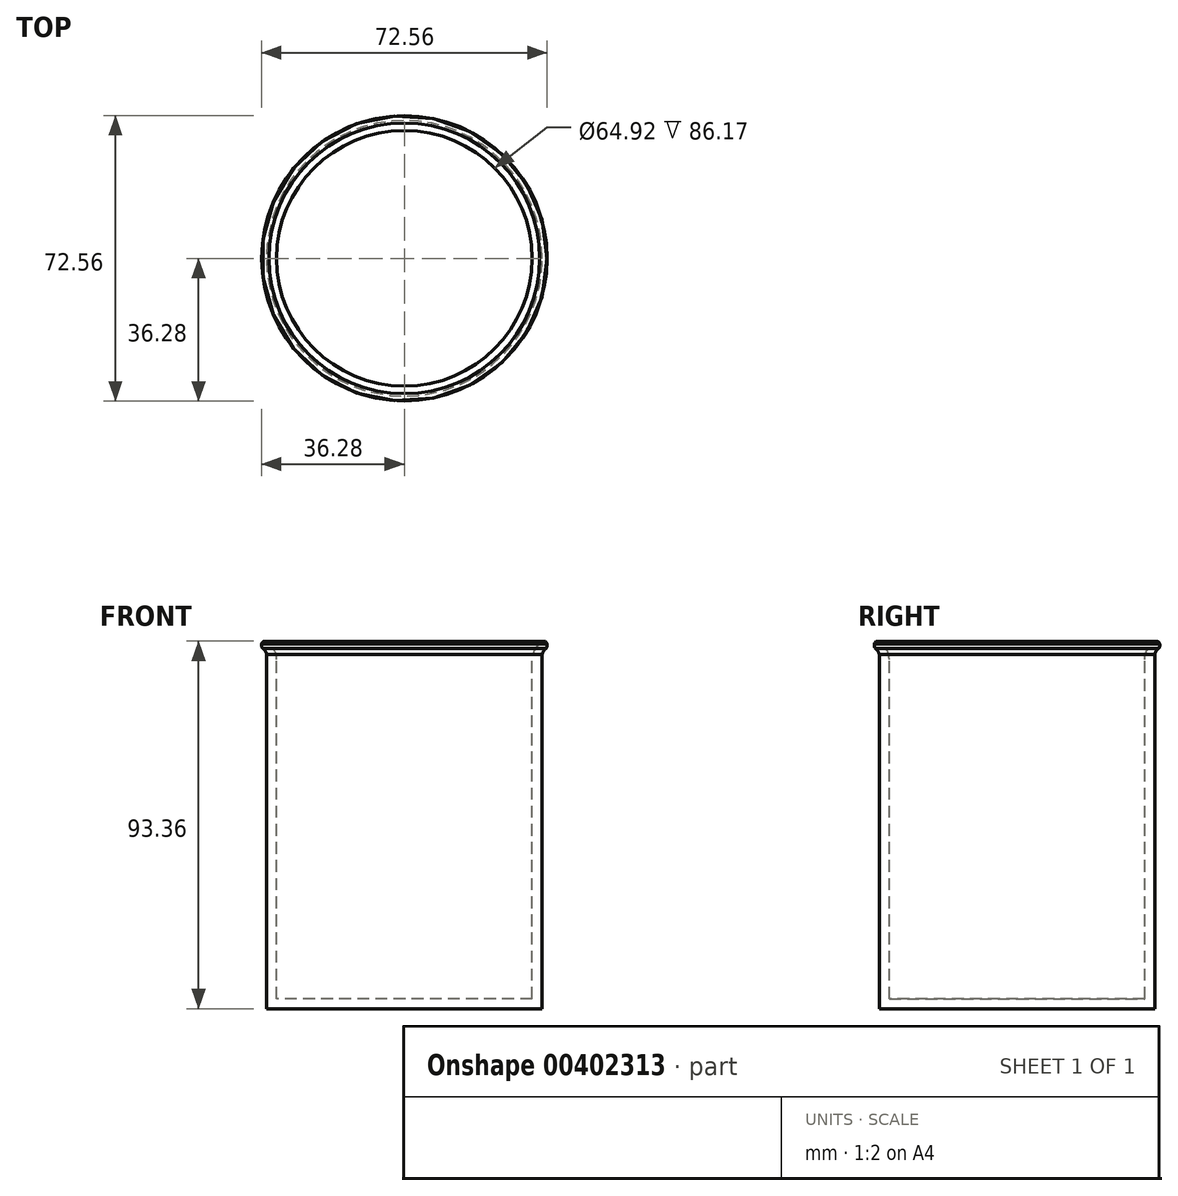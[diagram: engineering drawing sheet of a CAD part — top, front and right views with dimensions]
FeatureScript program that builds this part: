
annotation { "Feature Type Name" : "Feature", "Feature Type Description" : "" }
export const myFeature = defineFeature(function(context is Context, id is Id, definition is map)
    precondition{}
    {
        {
            var Q0;
            Q0=qCreatedBy(makeId("Front.planeOp"),FACE);
            var sketch = newSketch(context, id + "F0", { "sketchPlane" : qUnion([Q0])});
            skLineSegment(sketch, "E0.0", {"start": v(0, 45) * mm, "end": v(35, 45) * mm});
            skPoint(sketch, "E1", {"position": v(0, 45) * mm});
            skFitSpline(sketch, "E2", {"points": [v(35, 45) * mm, v(35.3, 45.79) * mm, v(35.98, 46.5) * mm], "startDerivative": vector(0.03, 0.4) * mm, "endDerivative": vector(0.23, 0.06) * mm});
            skLineSegment(sketch, "E3", {"start": v(35.98, 46.5) * mm, "end": v(0, 46.5) * mm});
            skLineSegment(sketch, "E4", {"start": v(0, 46.5) * mm, "end": v(0, 45) * mm});
            skFitSpline(sketch, "E5", {"points": [v(35.98, 46.5) * mm, v(36.23, 46.97) * mm, v(36.25, 47.7) * mm], "startDerivative": vector(0.12, 0.14) * mm, "endDerivative": vector(-0.1, 0.12) * mm});
            skPoint(sketch, "E6.endSnap0", {"position": v(18, 46.5) * mm});
            skLineSegment(sketch, "E7", {"start": v(34.4, 47.7) * mm, "end": v(0, 47.7) * mm});
            skLineSegment(sketch, "E8", {"start": v(0, 47.7) * mm, "end": v(0, 46.5) * mm});
            skFitSpline(sketch, "E9", {"points": [v(34.4, 47.7) * mm, v(34.6, 48.2) * mm, v(35.86, 48.26) * mm, v(36.25, 47.7) * mm], "startDerivative": vector(0.9, 3.73) * mm, "endDerivative": vector(0.6, -1) * mm});
            skLineSegment(sketch, "E10.0", {"start": v(0, -45) * mm, "end": v(35, -45) * mm});
            skLineSegment(sketch, "E11", {"start": v(35, -45) * mm, "end": v(0, -45) * mm});
            skLineSegment(sketch, "E12", {"start": v(0, -45) * mm, "end": v(0, 45) * mm});
            skLineSegment(sketch, "E13", {"start": v(35, 45) * mm, "end": v(35, -45) * mm});
            skSolve(sketch);
        }
        {
            var Q0;
            Q0 = qSketchRegion(id + "F0", true);
            var Q1;
            Q1=sQuery(id+"F0.wireOp",EDGE,"E4");
            revolve(context, id + "F1", {"entities" : qUnion([Q0]), "axis" : qUnion([Q1]), "revolveType" : RevolveType.ONE_DIRECTION, "angle" : 360 * degree});
        }
        {
            var Q0;
            Q0=makeQuery(id+"F1.opRevolve","SWEPT_FACE",FACE,{"disambiguationData":[OSD([sQuery(id+"F0.wireOp",EDGE,"E7")])]});
            shell(context, id + "F2", {"entities" : qUnion([Q0]), "thickness" : 2.54 * mm});
        }
        {
            var Q0;
            Q0=makeQuery(id+"F2.opShell","TWEAK_EDGE",EDGE,{"derivedFrom":[makeQuery(id+"F1.opRevolve","SWEPT_FACE",FACE,{"disambiguationData":[OSD([sQuery(id+"F0.wireOp",EDGE,"E2")])]}),makeQuery(id+"F1.opRevolve","SWEPT_FACE",FACE,{"disambiguationData":[OSD([sQuery(id+"F0.wireOp",EDGE,"E7")])]})]});
            fillet(context, id + "F3", {"entities" : qUnion([Q0]), "radius" : 5.08 * mm, "tangentPropagation" : true, "allowEdgeOverflow" : false});
        }
    });
